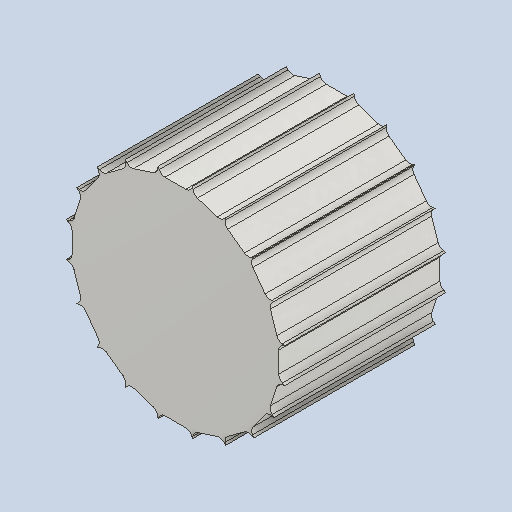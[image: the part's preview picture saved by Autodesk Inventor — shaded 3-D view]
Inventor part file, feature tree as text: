
AUTODESK INVENTOR PART (.ipt)
format: ipt  version: 2024 (Build 280153000, 153)  size: 237,568 bytes
history: native  units: mm (DEFAULTED — no unit token found)
features: other x3, extrude x2, fillet x1, pattern_circular x1
ambient origin geometry x8: Origin, YZ Plane, XZ Plane, XY Plane, X Axis, Y Axis, Z Axis, Center Point
bodies: Solid1 (feature_tree)
feature tree (7):
  other  "Pulley Sketch"
  extrude  "Base Body"  Depth=15.915494mm
  extrude  "Tooth"  Depth=0.3mm
  fillet  "Tooth Fillet"  Radius=1.25mm
  pattern_circular  "Teeth"  [2 undecoded]
  other  "Left flange"
  other  "Right flange"
note: 2 required parameter values undecoded (feature->parameter linkage not recoverable at this tier; creation-order binding heuristic only, values carry confidence <= 0.55)
